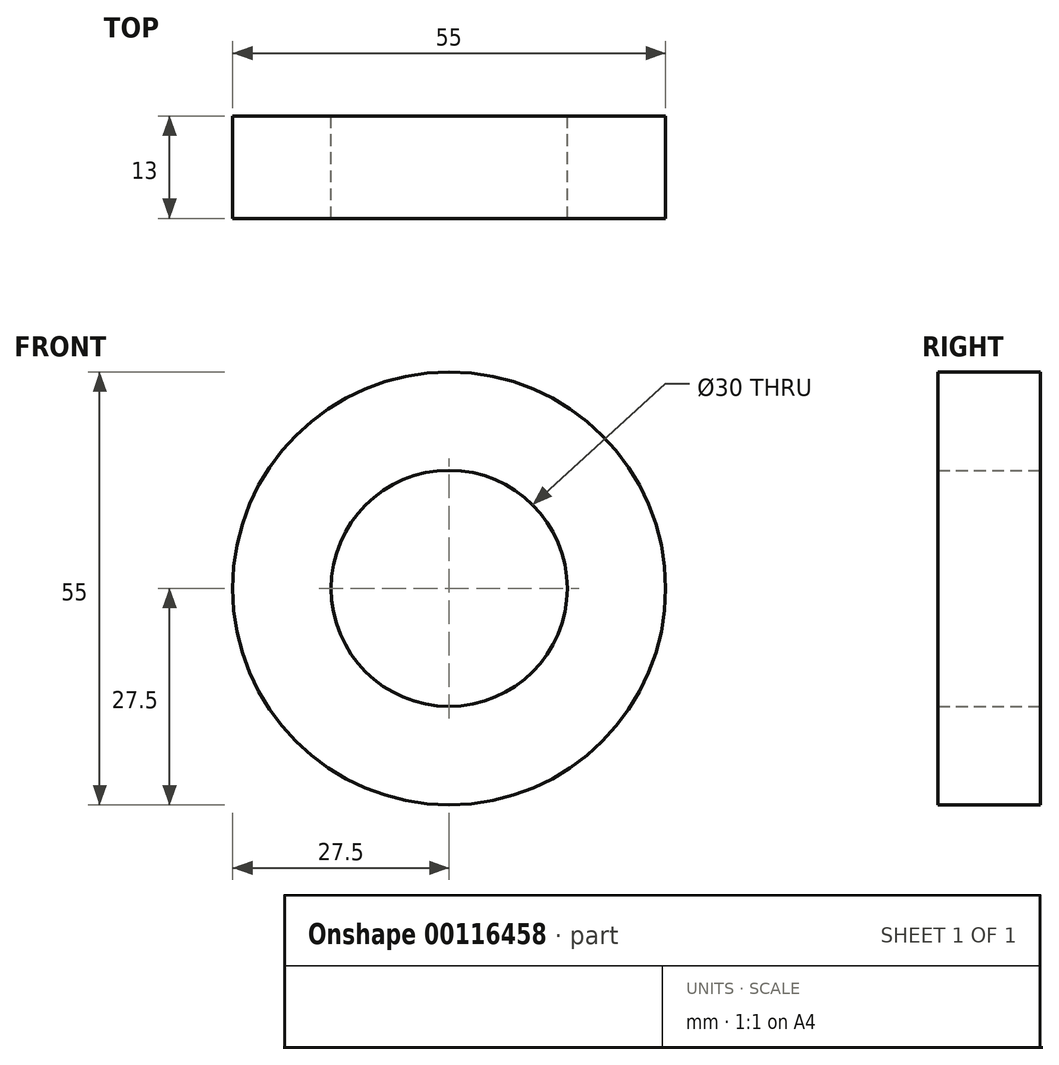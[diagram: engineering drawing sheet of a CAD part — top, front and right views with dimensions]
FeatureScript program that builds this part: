
annotation { "Feature Type Name" : "Feature", "Feature Type Description" : "" }
export const myFeature = defineFeature(function(context is Context, id is Id, definition is map)
    precondition{}
    {
        {
            var Q0;
            Q0=qCreatedBy(makeId("Front.planeOp"),FACE);
            var sketch = newSketch(context, id + "F0", { "sketchPlane" : qUnion([Q0])});
            skCircle(sketch, "E0", {"center": v(0, 0) * mm, "radius": 15 * mm});
            skCircle(sketch, "E1", {"center": v(0, 0) * mm, "radius": 27.5 * mm});
            skSolve(sketch);
        }
        {
            var Q0;
            Q0=makeQuery(id+"F0.imprint","IMPRINT",FACE,{"disambiguationData":[TD([[makeQuery(id+"F0.imprint","IMPRINT",EDGE,{"derivedFrom":sQuery(id+"F0.wireOp",EDGE,"E0")}),-1.0]])]});
            extrude(context, id + "F1", {"entities" : qUnion([Q0]), "depth" : 13 * mm});
        }
    });
